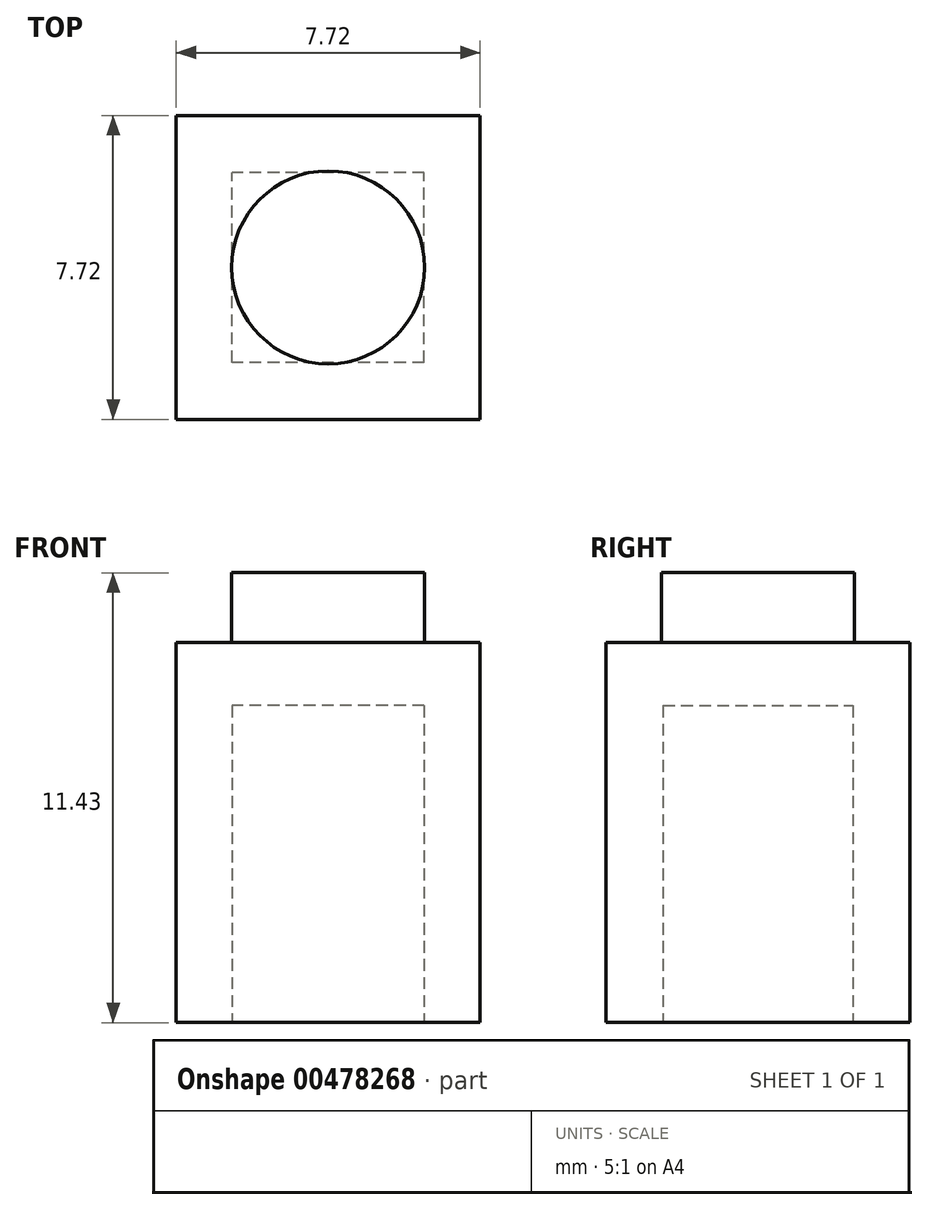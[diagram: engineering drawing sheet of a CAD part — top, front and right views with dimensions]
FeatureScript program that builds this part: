
annotation { "Feature Type Name" : "Feature", "Feature Type Description" : "" }
export const myFeature = defineFeature(function(context is Context, id is Id, definition is map)
    precondition{}
    {
        {
            var Q0;
            Q0=qCreatedBy(makeId("Top.planeOp"),FACE);
            var sketch = newSketch(context, id + "F0", { "sketchPlane" : qUnion([Q0])});
            skLineSegment(sketch, "E0.bottom", {"start": v(3.86, 3.86) * mm, "end": v(-3.86, 3.86) * mm});
            skLineSegment(sketch, "E0.top", {"start": v(3.86, -3.86) * mm, "end": v(-3.86, -3.86) * mm});
            skLineSegment(sketch, "E0.left", {"start": v(3.86, 3.86) * mm, "end": v(3.86, -3.86) * mm});
            skLineSegment(sketch, "E0.right", {"start": v(-3.86, 3.86) * mm, "end": v(-3.86, -3.86) * mm});
            skPoint(sketch, "E0.middle", {"position": v(0, 0) * mm});
            skSolve(sketch);
        }
        {
            var Q0;
            Q0 = qSketchRegion(id + "F0", true);
            extrude(context, id + "F1", {"entities" : qUnion([Q0]), "endBound" : BoundingType.SYMMETRIC, "depth" : 9.65 * mm, "offsetDistance" : 25.4 * mm});
        }
        {
            var Q0;
            Q0=makeQuery(id+"F1.opExtrude","CAP_FACE",FACE,{"disambiguationData":[OSD([sQuery(id+"F0.wireOp",EDGE,"E0.bottom"),sQuery(id+"F0.wireOp",EDGE,"E0.top"),sQuery(id+"F0.wireOp",EDGE,"E0.left"),sQuery(id+"F0.wireOp",EDGE,"E0.right")])],"isStart":false});
            var sketch = newSketch(context, id + "F2", { "sketchPlane" : qUnion([Q0])});
            skCircle(sketch, "E1", {"center": v(0, 0) * mm, "radius": 2.45 * mm});
            skSolve(sketch);
        }
        {
            var Q0;
            Q0 = qSketchRegion(id + "F2", true);
            extrude(context, id + "F3", {"entities" : qUnion([Q0]), "operationType" : NewBodyOperationType.ADD, "depth" : 1.78 * mm, "offsetDistance" : 25.4 * mm});
        }
        {
            var Q0;
            Q0=makeQuery(id+"F1.opExtrude","CAP_FACE",FACE,{"disambiguationData":[OSD([sQuery(id+"F0.wireOp",EDGE,"E0.bottom"),sQuery(id+"F0.wireOp",EDGE,"E0.top"),sQuery(id+"F0.wireOp",EDGE,"E0.left"),sQuery(id+"F0.wireOp",EDGE,"E0.right")])],"isStart":true});
            var sketch = newSketch(context, id + "F4", { "sketchPlane" : qUnion([Q0])});
            skLineSegment(sketch, "E2.bottom", {"start": v(2.44, 2.41) * mm, "end": v(-2.44, 2.41) * mm});
            skLineSegment(sketch, "E2.top", {"start": v(2.44, -2.41) * mm, "end": v(-2.44, -2.41) * mm});
            skLineSegment(sketch, "E2.left", {"start": v(2.44, 2.41) * mm, "end": v(2.44, -2.41) * mm});
            skLineSegment(sketch, "E2.right", {"start": v(-2.44, 2.41) * mm, "end": v(-2.44, -2.41) * mm});
            skPoint(sketch, "E2.middle", {"position": v(0, 0) * mm});
            skSolve(sketch);
        }
        {
            var Q0;
            Q0=makeQuery(id+"F4.imprint","IMPRINT",FACE,{"disambiguationData":[TD([[makeQuery(id+"F4.imprint","IMPRINT",EDGE,{"derivedFrom":sQuery(id+"F4.wireOp",EDGE,"E2.bottom")}),1.0]])]});
            extrude(context, id + "F5", {"entities" : qUnion([Q0]), "operationType" : NewBodyOperationType.REMOVE, "oppositeDirection" : true, "depth" : 8.05 * mm, "offsetDistance" : 25.4 * mm});
        }
    });
